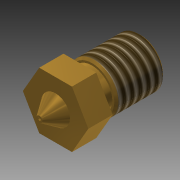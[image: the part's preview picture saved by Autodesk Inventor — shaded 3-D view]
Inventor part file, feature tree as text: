
AUTODESK INVENTOR PART (.ipt)
format: ipt  version: 2015 (Build 190159000, 159)  size: 148,992 bytes
history: native  units: mm
features: sketch x4, hole x3, chamfer x2, other x1, revolve x1, thread x1, extrude x1
ambient origin geometry x8: Origin, YZ Plane, XZ Plane, XY Plane, X Axis, Y Axis, Z Axis, Center Point
bodies: Body1 (feature_tree)
feature tree (13):
  other  "Твердое тело1"
  revolve  "Вращение1"
  chamfer  "Фаска1"  Distance=15.0mm
  thread  "Резьба1"
  sketch  "Эскиз2"
  sketch  "Эскиз3"
  hole  "Отверстие1"  [1 undecoded]
  hole  "Отверстие2"  [1 undecoded]
  chamfer  "Фаска2"  Distance=7.5mm
  hole  "Отверстие3"  [1 undecoded]
  extrude  "Выдавливание1"  Depth=5.0mm
  sketch  "Эскиз1"
  sketch  "Эскиз4"
note: 3 required parameter values undecoded (feature->parameter linkage not recoverable at this tier; creation-order binding heuristic only, values carry confidence <= 0.55)
